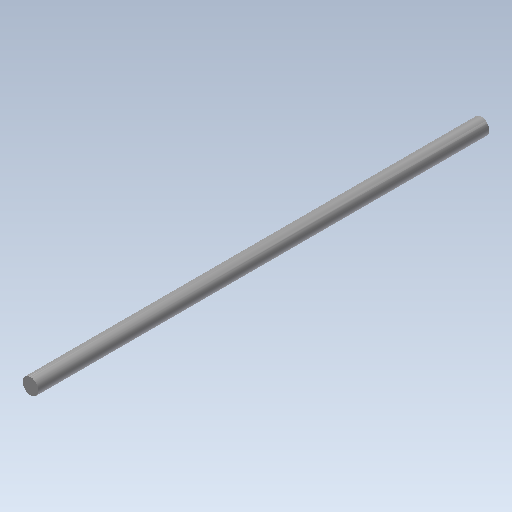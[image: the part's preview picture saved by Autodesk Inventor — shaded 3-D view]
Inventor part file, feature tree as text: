
AUTODESK INVENTOR PART (.ipt)
format: ipt  version: 2021.3 (Build 253353000, 353)  size: 95,232 bytes
history: native  units: mm
features: extrude x1, sketch x1
ambient origin geometry x8: Origin, YZ Plane, XZ Plane, XY Plane, X Axis, Y Axis, Z Axis, Center Point
bodies: Solid1 (feature_tree)
feature tree (2):
  extrude  "Extrusion1"  Depth=340.0mm TaperAngle=0.0deg
  sketch  "Sketch1"  dims[d0=12.0mm d1=340.0mm d2=0.0mm]
